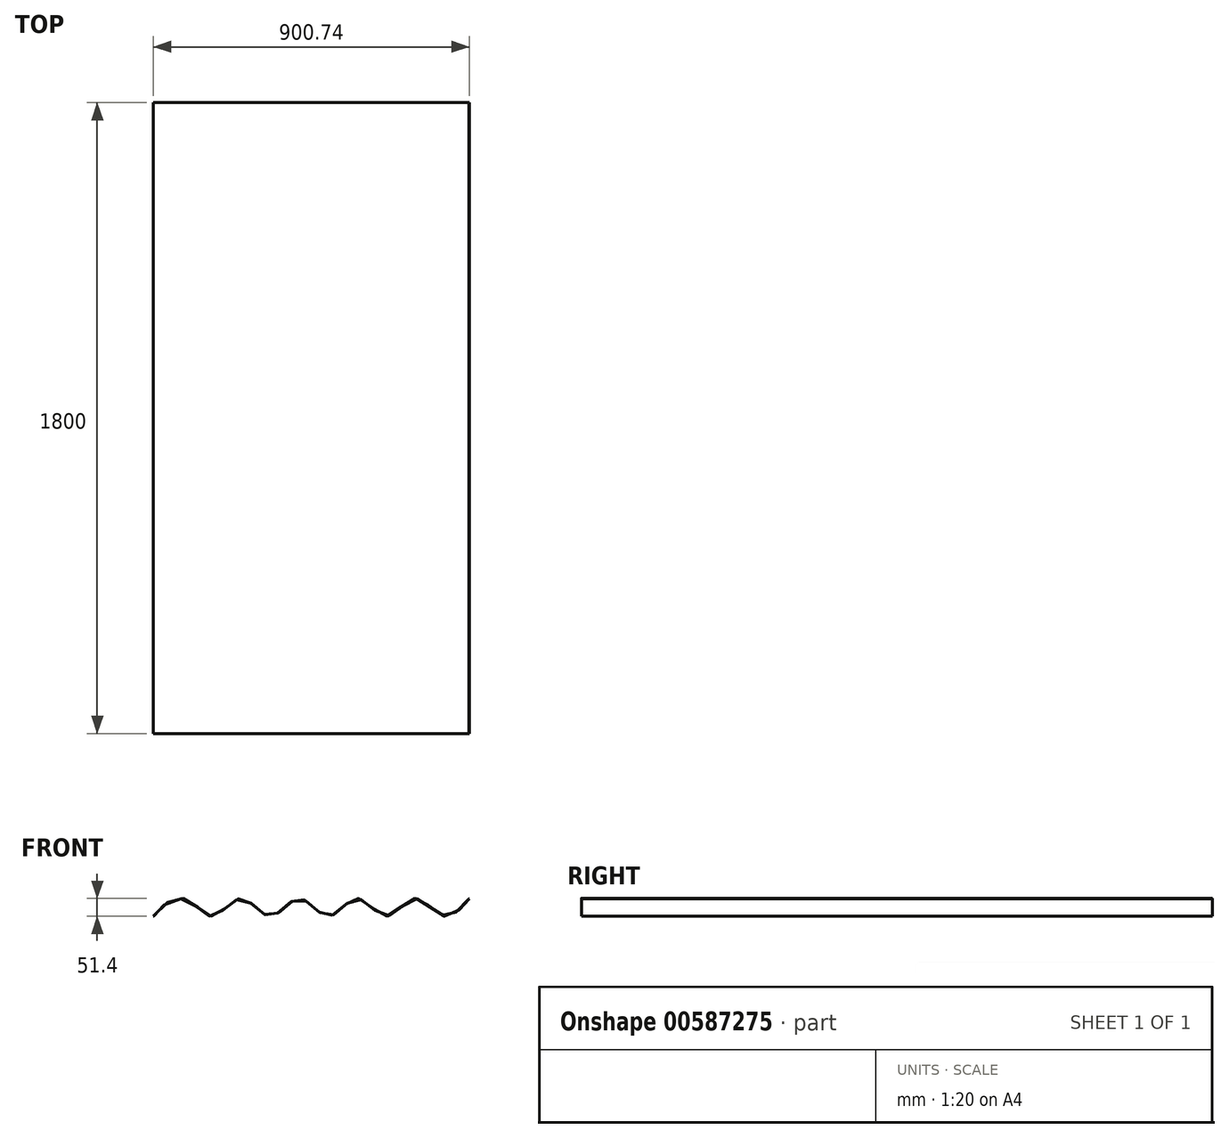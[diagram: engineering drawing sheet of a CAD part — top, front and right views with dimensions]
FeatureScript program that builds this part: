
annotation { "Feature Type Name" : "Feature", "Feature Type Description" : "" }
export const myFeature = defineFeature(function(context is Context, id is Id, definition is map)
    precondition{}
    {
        {
            var Q0;
            Q0=qCreatedBy(makeId("Front.planeOp"),FACE);
            var sketch = newSketch(context, id + "F0", { "sketchPlane" : qUnion([Q0])});
            skFitSpline(sketch, "E0", {"points": [v(-498, 0) * mm, v(-415, 50) * mm, v(-332, 0) * mm, v(-249, 50) * mm, v(-166, 0) * mm, v(-83, 50) * mm, v(0, 0) * mm, v(83, 50) * mm, v(166, 0) * mm, v(249, 50) * mm, v(332, 0) * mm, v(402, 50) * mm], "startDerivative": vector(231.53, 562.7) * mm, "endDerivative": vector(363.1, 536.47) * mm});
            skFitSpline(sketch, "E1.0", {"points": [v(-498.74, 0.3) * mm, v(-498.11, 1.83) * mm, v(-496.34, 5.13) * mm, v(-490.96, 12.55) * mm, v(-481.18, 22.84) * mm, v(-468.44, 32.97) * mm, v(-457.14, 40.05) * mm, v(-448.28, 44.61) * mm, v(-439.2, 48.2) * mm, v(-431.57, 50.17) * mm, v(-425.52, 51.02) * mm, v(-421.03, 51.26) * mm, v(-416.6, 51.07) * mm, v(-412.27, 50.42) * mm, v(-408.05, 49.32) * mm, v(-402.56, 47.33) * mm, v(-395.96, 43.95) * mm, v(-388.38, 38.85) * mm, v(-378.68, 31.08) * mm, v(-369.46, 22.55) * mm, v(-360.54, 14.62) * mm, v(-353.97, 9.31) * mm, v(-347.47, 4.97) * mm, v(-342.1, 2.44) * mm, v(-337.8, 1.23) * mm, v(-334.6, 0.75) * mm, v(-331.37, 0.76) * mm, v(-328.1, 1.26) * mm, v(-324.8, 2.23) * mm, v(-320.32, 4.08) * mm, v(-314.62, 7.34) * mm, v(-307.67, 12.42) * mm, v(-300.62, 18.3) * mm, v(-293.5, 24.62) * mm, v(-286.31, 31) * mm, v(-279.08, 37.1) * mm, v(-271.8, 42.53) * mm, v(-264.48, 46.93) * mm, v(-258.34, 49.44) * mm, v(-253.4, 50.55) * mm, v(-249.69, 50.9) * mm, v(-245.97, 50.67) * mm, v(-242.28, 49.93) * mm, v(-238.61, 48.72) * mm, v(-233.76, 46.57) * mm, v(-227.74, 42.96) * mm, v(-220.57, 37.57) * mm, v(-213.45, 31.48) * mm, v(-206.36, 25.06) * mm, v(-199.3, 18.69) * mm, v(-192.27, 12.74) * mm, v(-185.26, 7.58) * mm, v(-179.46, 4.25) * mm, v(-174.85, 2.34) * mm, v(-171.41, 1.34) * mm, v(-167.99, 0.8) * mm, v(-164.58, 0.76) * mm, v(-161.16, 1.25) * mm, v(-156.56, 2.52) * mm, v(-150.77, 5.18) * mm, v(-143.76, 9.75) * mm, v(-136.7, 15.31) * mm, v(-129.63, 21.5) * mm, v(-122.53, 27.96) * mm, v(-115.41, 34.29) * mm, v(-108.27, 40.12) * mm, v(-101.1, 45.08) * mm, v(-95.09, 48.18) * mm, v(-90.24, 49.84) * mm, v(-86.6, 50.63) * mm, v(-82.92, 50.9) * mm, v(-79.25, 50.6) * mm, v(-75.6, 49.79) * mm, v(-70.76, 48.1) * mm, v(-64.75, 44.96) * mm, v(-57.59, 39.96) * mm, v(-50.46, 34.11) * mm, v(-40.98, 25.66) * mm, v(-31.54, 16.99) * mm, v(-22.14, 9.6) * mm, v(-15.12, 5.06) * mm, v(-9.32, 2.44) * mm, v(-4.71, 1.2) * mm, v(-1.28, 0.75) * mm, v(2.14, 0.82) * mm, v(5.59, 1.4) * mm, v(9.05, 2.43) * mm, v(13.68, 4.37) * mm, v(19.52, 7.75) * mm, v(26.56, 12.96) * mm, v(33.63, 18.94) * mm, v(40.72, 25.34) * mm, v(47.83, 31.76) * mm, v(54.95, 37.84) * mm, v(62.1, 43.2) * mm, v(68.08, 46.76) * mm, v(72.9, 48.87) * mm, v(76.53, 50.03) * mm, v(80.18, 50.72) * mm, v(83.85, 50.88) * mm, v(87.5, 50.48) * mm, v(92.35, 49.28) * mm, v(98.37, 46.66) * mm, v(105.53, 42.13) * mm, v(115.03, 34.74) * mm, v(124.5, 26.08) * mm, v(133.93, 17.64) * mm, v(141, 11.79) * mm, v(148.04, 6.8) * mm, v(153.88, 3.66) * mm, v(158.52, 1.94) * mm, v(161.99, 1.1) * mm, v(165.44, 0.72) * mm, v(168.88, 0.88) * mm, v(172.35, 1.52) * mm, v(177, 2.98) * mm, v(182.86, 5.84) * mm, v(189.95, 10.57) * mm, v(199.42, 18.12) * mm, v(208.92, 26.8) * mm, v(218.41, 35.13) * mm, v(225.53, 40.84) * mm, v(232.65, 45.64) * mm, v(238.6, 48.57) * mm, v(243.37, 50.08) * mm, v(246.36, 50.63) * mm, v(248.76, 50.82) * mm, v(251.16, 50.81) * mm, v(254.14, 50.48) * mm, v(257.69, 49.6) * mm, v(262.39, 47.84) * mm, v(268.22, 44.7) * mm, v(275.17, 39.75) * mm, v(282.12, 34) * mm, v(289.1, 27.78) * mm, v(296.1, 21.46) * mm, v(303.17, 15.38) * mm, v(310.3, 9.9) * mm, v(317.53, 5.35) * mm, v(323.61, 2.64) * mm, v(328.53, 1.28) * mm, v(332.23, 0.7) * mm, v(335.98, 0.6) * mm, v(341.03, 1.07) * mm, v(347.4, 2.7) * mm, v(355.03, 6.05) * mm, v(362.53, 10.54) * mm, v(369.77, 15.9) * mm, v(376.64, 21.84) * mm, v(385.16, 30.18) * mm, v(394.32, 40.68) * mm, v(399.46, 47.68) * mm, v(401.34, 50.45) * mm]});
            skLineSegment(sketch, "E2", {"start": v(-498.74, 0.3) * mm, "end": v(-498, 0) * mm});
            skLineSegment(sketch, "E3", {"start": v(402, 50) * mm, "end": v(401.34, 50.45) * mm});
            skSolve(sketch);
        }
        {
            var Q0;
            Q0=makeQuery(id+"F0.imprint","IMPRINT",FACE,{"disambiguationData":[TD([[makeQuery(id+"F0.imprint","IMPRINT",EDGE,{"derivedFrom":sQuery(id+"F0.wireOp",EDGE,"E0")}),1.0]])]});
            extrude(context, id + "F1", {"entities" : qUnion([Q0]), "endBound" : BoundingType.SYMMETRIC, "depth" : 1800 * mm, "offsetDistance" : 25 * mm});
        }
    });
